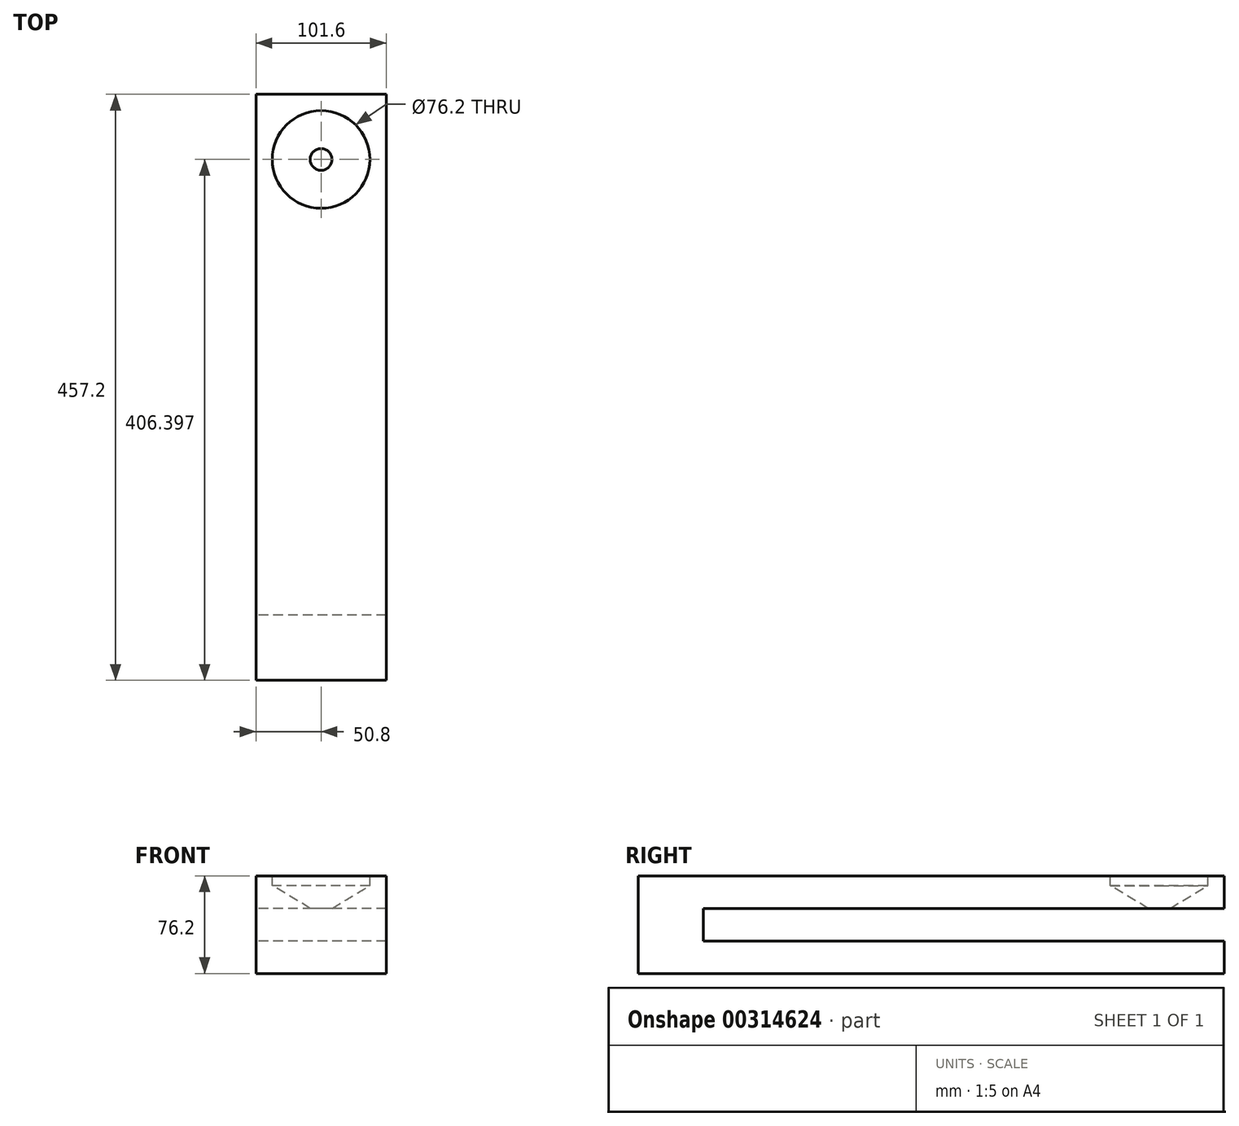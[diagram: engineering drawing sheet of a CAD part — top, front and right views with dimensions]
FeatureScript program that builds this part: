
annotation { "Feature Type Name" : "Feature", "Feature Type Description" : "" }
export const myFeature = defineFeature(function(context is Context, id is Id, definition is map)
    precondition{}
    {
        {
            var Q0;
            Q0=qCreatedBy(makeId("Right.planeOp"),FACE);
            var sketch = newSketch(context, id + "F0", { "sketchPlane" : qUnion([Q0])});
            skLineSegment(sketch, "E0", {"start": v(-171.82, 50.8) * mm, "end": v(-171.82, -25.4) * mm});
            skLineSegment(sketch, "E1", {"start": v(-171.82, -25.4) * mm, "end": v(285.38, -25.4) * mm});
            skLineSegment(sketch, "E2", {"start": v(285.38, -25.4) * mm, "end": v(285.38, 0) * mm});
            skLineSegment(sketch, "E3", {"start": v(285.38, 0) * mm, "end": v(-121.02, 0) * mm});
            skLineSegment(sketch, "E4", {"start": v(-121.02, 0) * mm, "end": v(-121.02, 25.4) * mm});
            skLineSegment(sketch, "E5", {"start": v(-121.02, 25.4) * mm, "end": v(285.38, 25.4) * mm});
            skLineSegment(sketch, "E6", {"start": v(285.38, 25.4) * mm, "end": v(285.38, 50.8) * mm});
            skLineSegment(sketch, "E7", {"start": v(285.38, 50.8) * mm, "end": v(-171.82, 50.8) * mm});
            skSolve(sketch);
        }
        {
            var Q0;
            Q0=makeQuery(id+"F0.imprint","IMPRINT",FACE,{"disambiguationData":[TD([[makeQuery(id+"F0.imprint","IMPRINT",EDGE,{"derivedFrom":sQuery(id+"F0.wireOp",EDGE,"E0")}),1.0]])]});
            extrude(context, id + "F1", {"entities" : qUnion([Q0]), "endBound" : BoundingType.SYMMETRIC, "depth" : 101.6 * mm});
        }
        {
            var Q0;
            Q0=makeQuery(id+"F1.opExtrude","SWEPT_FACE",FACE,{"disambiguationData":[OSD([sQuery(id+"F0.wireOp",EDGE,"E7")])]});
            var sketch = newSketch(context, id + "F2", { "sketchPlane" : qUnion([Q0])});
            skCircle(sketch, "E8", {"center": v(0, 234.58) * mm, "radius": 38.1 * mm});
            skSolve(sketch);
        }
        {
            var Q0;
            Q0=sQuery(id+"F2.wireOp",VERTEX,"E8.center");
            var Q1;
            Q1=makeQuery(id+"F1.opExtrude","SWEPT_BODY",BODY,{"disambiguationData":[OSD([sQuery(id+"F0.wireOp",EDGE,"E0"),sQuery(id+"F0.wireOp",EDGE,"E1"),sQuery(id+"F0.wireOp",EDGE,"E2"),sQuery(id+"F0.wireOp",EDGE,"E3"),sQuery(id+"F0.wireOp",EDGE,"E4"),sQuery(id+"F0.wireOp",EDGE,"E5"),sQuery(id+"F0.wireOp",EDGE,"E6"),sQuery(id+"F0.wireOp",EDGE,"E7")])]});
            hole(context, id + "F3", {"style" : HoleStyle.SIMPLE, "endStyle" : HoleEndStyle.BLIND, "holeDiameter" : 76.2 * mm, "holeDepth" : 7.62 * mm, "tappedDepth" : 12.7 * mm, "tapClearance" : 3, "locations" : qUnion([Q0]), "scope" : qUnion([Q1])});
        }
    });
